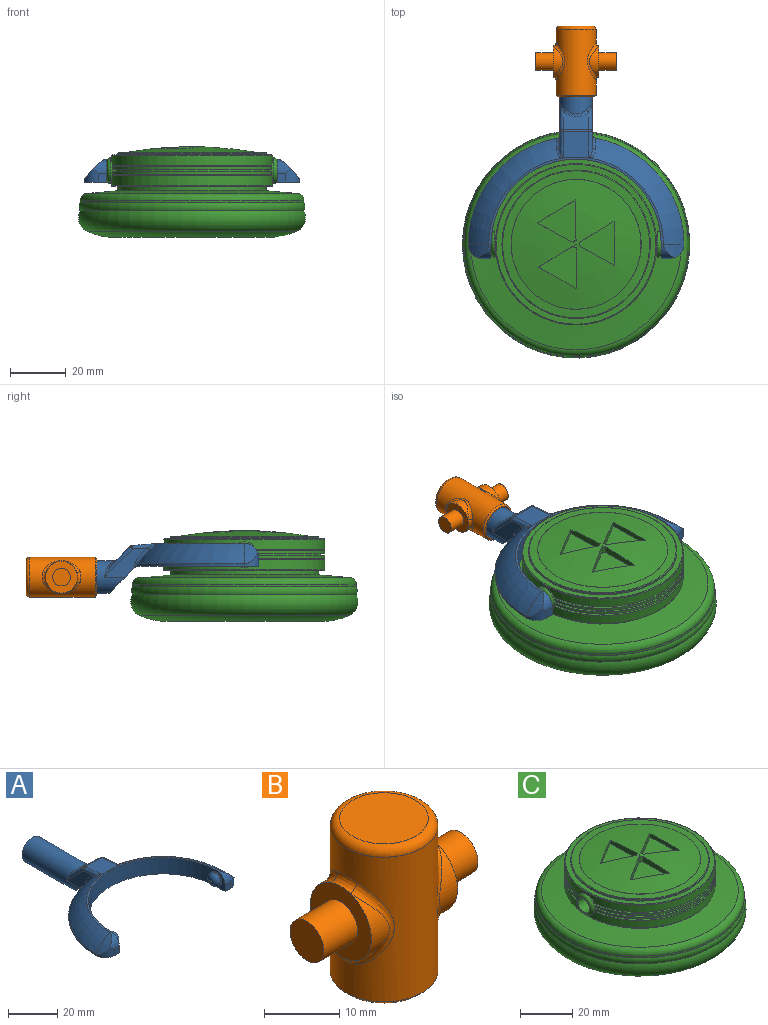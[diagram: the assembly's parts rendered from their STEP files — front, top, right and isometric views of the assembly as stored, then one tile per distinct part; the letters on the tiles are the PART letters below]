
ASSEMBLY  parts=3 mates=2
PART A: 48 faces, bbox 77.3x80.8x18.2 mm
  f0: plane 11.99x9.83mm, normal (0,-0.71,-0.71), area 141.5mm2, adj f1,f2,f9,f30,f43,f46
  f1: plane 15.39x10.49mm, normal (-1,0,0), area 63.5mm2, adj f0,f30,f32,f36,f46,f47
  f2: plane 15.39x10.49mm, normal (1,0,0), area 63.5mm2, adj f0,f30,f34,f39,f43,f44
  f3: plane 9.14x6.37mm, normal (0,0.71,0.71), area 67.6mm2, adj f35,f36,f39,f40
  f4: cylinder r=38.61mm len=37.99mm, axis (0,0,-1), area 42.6mm2, adj f6,f9,f17,f46,f47
  f5: torus R=19.3mm, axis (0,0,-1), area 507.8mm2, adj f10,f11,f12,f29,f42,f44
  f6: torus R=19.3mm, axis (0,0,-1), area 507.8mm2, adj f4,f11,f15,f28,f45,f47
  f7: cylinder r=30.48mm len=60.96mm, axis (0,0,-1), area 746.6mm2, adj f8,f9,f11,f14,f21,f24
  f8: plane 8.13x5.08mm, normal (-1,0,0), area 19.9mm2, adj f7,f9,f13,f19,f24
  f9: plane 77.22x43.73mm, normal (0,0,-1), area 956.2mm2, adj f0,f4,f7,f8,f10,f13,f14,f16
  f10: cylinder r=38.61mm len=37.99mm, axis (0,0,-1), area 42.6mm2, adj f5,f9,f20,f43,f44
  f11: plane 62.55x30.95mm, normal (0,0,1), area 75mm2, adj f5,f6,f7,f18,f19,f27
  f12: cylinder r=22.71mm len=7.33mm, axis (0,1,0), area 24.8mm2, adj f5,f19,f20
  f13: plane 3.05x3.05mm, normal (0,-1,0), area 9.3mm2, adj f8,f9,f19,f20
  f14: plane 8.13x5.08mm, normal (1,0,0), area 19.9mm2, adj f7,f9,f16,f18,f21
  f15: cylinder r=22.71mm len=7.33mm, axis (0,1,0), area 24.8mm2, adj f6,f17,f18
  f16: plane 3.05x3.05mm, normal (0,-1,0), area 9.3mm2, adj f9,f14,f17,f18
  f17: cylinder r=5.08mm len=5.08mm, axis (0,0,-1), area 21.9mm2, adj f4,f9,f15,f16,f18
  f18: cylinder r=5.08mm len=5.08mm, axis (-1,0,0), area 21.9mm2, adj f11,f14,f15,f16,f17
  f19: cylinder r=5.08mm len=5.08mm, axis (-1,0,0), area 21.9mm2, adj f8,f11,f12,f13,f20
  f20: cylinder r=5.08mm len=5.08mm, axis (0,0,-1), area 21.9mm2, adj f9,f10,f12,f13,f19
  f21: cylinder r=3.17mm len=6.35mm, axis (-1,0,0), area 12.7mm2, adj f7,f14,f23
  f22: plane 1.27x1.27mm, normal (1,0,0), area 1.3mm2, adj f23
  f23: torus R=0.64mm, axis (1,0,0), area 56.5mm2, adj f21,f22
  f24: cylinder r=3.17mm len=6.35mm, axis (1,0,0), area 12.7mm2, adj f7,f8,f26
  f25: plane 1.27x1.27mm, normal (-1,0,0), area 1.3mm2, adj f26
  f26: torus R=0.64mm, axis (-1,0,0), area 56.5mm2, adj f24,f25
  f27: plane 9.86x9.36mm, normal (0,0.09,1), area 85.6mm2, adj f11,f28,f29,f32,f34,f35,f42,f45
  f28: plane 1.04x0.17mm, normal (0,-1,0), area 0mm2, adj f6,f27,f45
  f29: plane 1.04x0.17mm, normal (0,-1,0), area 0mm2, adj f5,f27,f42
  f30: cylinder r=5.84mm len=33.01mm, axis (0,-1,0), area 1029.7mm2, adj f0,f1,f2,f31,f38,f40,f41
  f31: plane 11.68x11.68mm, normal (0,1,0), area 107.2mm2, adj f30
  f32: cylinder r=1.27mm len=9.13mm, axis (0,-1,0.09), area 14.4mm2, adj f1,f27,f33,f45
  f33: sphere r=1.27mm, area 1.5mm2, adj f32,f35,f36
  f34: cylinder r=1.27mm len=9.13mm, axis (0,1,-0.09), area 14.4mm2, adj f2,f27,f37,f42
  f35: cylinder r=1.27mm len=9.14mm, axis (-1,0,0), area 8.1mm2, adj f3,f27,f33,f37
  f36: cylinder r=1.27mm len=10.91mm, axis (0,-0.71,0.71), area 23.1mm2, adj f1,f3,f33,f38
  f37: sphere r=1.27mm, area 1.5mm2, adj f34,f35,f39
  f38: bspline ~4.55x2.75mm, area 2.3mm2, adj f30,f36,f40
  f39: cylinder r=1.27mm len=10.91mm, axis (0,0.71,-0.71), area 23.1mm2, adj f2,f3,f37,f41
  f40: bspline ~9.14x2.56mm, area 10.7mm2, adj f3,f30,f38,f41
  f41: bspline ~5.23x3.53mm, area 2.3mm2, adj f30,f39,f40
  f42: bspline ~4.62x3.14mm, area 5.2mm2, adj f5,f27,f29,f34,f44
  f43: cylinder r=1.27mm len=1.74mm, axis (0,0,-1), area 1.9mm2, adj f0,f2,f9,f10,f44
  f44: bspline ~8.6x7.86mm, area 11.9mm2, adj f2,f5,f10,f42,f43
  f45: bspline ~4.62x3.14mm, area 5.2mm2, adj f6,f27,f28,f32,f47
  f46: cylinder r=1.27mm len=1.74mm, axis (0,0,-1), area 1.9mm2, adj f0,f1,f4,f9,f47
  f47: bspline ~8.6x7.86mm, area 11.9mm2, adj f1,f4,f6,f45,f46
PART B: 25 faces, bbox 28.9x15.5x25.4 mm
  f0: cylinder r=5.71mm len=10.81mm, axis (-1,0,0), area 26.2mm2, adj f5,f15
  f1: cylinder r=5.71mm len=10.81mm, axis (-1,0,0), area 26.2mm2, adj f8,f11
  f2: cylinder r=7.14mm len=23.5mm, axis (0,0,-1), area 763.2mm2, adj f9,f10,f11,f12,f13,f14,f15,f16
  f3: plane 11.75x11.75mm, normal (0,0,1), area 108.4mm2, adj f17
  f4: plane 13.02x13.02mm, normal (0,0,-1), area 16.3mm2, adj f22,f24
  f5: plane 11.46x11.46mm, normal (1,0,0), area 70.9mm2, adj f0,f6,f13,f16,f18
  f6: cylinder r=5.71mm len=10.81mm, axis (-1,0,0), area 26.2mm2, adj f5,f14
  f7: cylinder r=5.71mm len=10.81mm, axis (-1,0,0), area 26.2mm2, adj f8,f10
  f8: plane 11.46x11.46mm, normal (-1,0,0), area 70.9mm2, adj f1,f7,f9,f12,f20
  f9: bspline ~4.64x1.73mm, area 6.5mm2, adj f2,f8,f10,f11
  f10: bspline ~13.62x4.91mm, area 20.7mm2, adj f2,f7,f9,f12
  f11: bspline ~13.6x4.87mm, area 20.7mm2, adj f1,f2,f9,f12
  f12: bspline ~4.64x1.73mm, area 6.5mm2, adj f2,f8,f10,f11
  f13: bspline ~4.64x1.73mm, area 6.5mm2, adj f2,f5,f14,f15
  f14: bspline ~13.62x4.91mm, area 20.7mm2, adj f2,f6,f13,f16
  f15: bspline ~13.6x4.87mm, area 20.7mm2, adj f0,f2,f13,f16
  f16: bspline ~4.64x1.73mm, area 6.5mm2, adj f2,f5,f14,f15
  f17: torus R=5.87mm, axis (0,0,1), area 83.8mm2, adj f2,f3
  f18: cylinder r=3.17mm len=6.35mm, axis (-1,0,0), area 126.7mm2, adj f5,f19
  f19: plane 6.35x6.35mm, normal (1,0,0), area 31.7mm2, adj f18
  f20: cylinder r=3.17mm len=6.35mm, axis (1,0,0), area 126.7mm2, adj f8,f21
  f21: plane 6.35x6.35mm, normal (-1,0,0), area 31.7mm2, adj f20
  f22: cylinder r=6.1mm len=22.86mm, axis (0,0,-1), area 875.6mm2, adj f4,f23
  f23: plane 12.19x12.19mm, normal (0,0,-1), area 116.7mm2, adj f22
  f24: cone r=7.14mm half-angle=45deg, axis (0,0,1), area 38.5mm2, adj f2,f4
PART C: 64 faces, bbox 96.2x96.2x32.5 mm
  f0: cylinder r=28.87mm len=57.73mm, axis (0,0,-1), area 603.9mm2, adj f1,f2,f54,f55,f60
  f1: plane 57.13x24.69mm, normal (0,0,1), area 102mm2, adj f0,f3,f54,f55
  f2: plane 57.13x24.69mm, normal (0,0,1), area 102mm2, adj f0,f4,f54,f55
  f3: cylinder r=27.6mm len=54.56mm, axis (0,0,1), area 49.6mm2, adj f1,f6,f54,f55
  f4: cylinder r=27.6mm len=54.56mm, axis (0,0,1), area 49.6mm2, adj f2,f5,f54,f55
  f5: plane 57.06x24.46mm, normal (0,0,-1), area 101.4mm2, adj f4,f7,f54,f55
  f6: plane 57.06x24.46mm, normal (0,0,-1), area 101.4mm2, adj f3,f8,f54,f55
  f7: cylinder r=28.87mm len=57.06mm, axis (0,0,-1), area 76.2mm2, adj f5,f10,f54,f55
  f8: cylinder r=28.87mm len=57.06mm, axis (0,0,-1), area 76.2mm2, adj f6,f9,f54,f55
  f9: plane 57.01x24.3mm, normal (0,0,1), area 101mm2, adj f8,f11,f54,f55
  f10: plane 57.01x24.3mm, normal (0,0,1), area 101mm2, adj f7,f12,f54,f55
  f11: cylinder r=27.6mm len=54.44mm, axis (0,0,1), area 49.2mm2, adj f9,f14,f54,f55
  f12: cylinder r=27.6mm len=54.44mm, axis (0,0,1), area 49.2mm2, adj f10,f13,f54,f55
  f13: plane 57.01x24.31mm, normal (0,0,-1), area 101mm2, adj f12,f15,f54,f55
  f14: plane 57.01x24.31mm, normal (0,0,-1), area 101mm2, adj f11,f16,f54,f55
  f15: cylinder r=28.87mm len=57.07mm, axis (0,0,-1), area 79.4mm2, adj f13,f18,f54,f55
  f16: cylinder r=28.87mm len=57.07mm, axis (0,0,-1), area 79.4mm2, adj f14,f17,f54,f55
  f17: plane 57.07x24.49mm, normal (0,0,1), area 101.5mm2, adj f16,f19,f54,f55
  f18: plane 57.07x24.49mm, normal (0,0,1), area 101.5mm2, adj f15,f20,f54,f55
  f19: cylinder r=27.6mm len=54.57mm, axis (0,0,1), area 49.6mm2, adj f17,f22,f54,f55
  f20: cylinder r=27.6mm len=54.57mm, axis (0,0,1), area 49.6mm2, adj f18,f21,f54,f55
  f21: plane 57.14x24.73mm, normal (0,0,-1), area 102.1mm2, adj f20,f23,f54,f55
  f22: plane 57.14x24.73mm, normal (0,0,-1), area 102.1mm2, adj f19,f23,f54,f55
  f23: cylinder r=28.87mm len=57.73mm, axis (0,0,-1), area 587.6mm2, adj f21,f22,f54,f55,f61
  f24: sphere r=135.39mm, area 1385.3mm2, adj f38,f39,f40,f41,f43,f44,f45,f46
  f25: plane 39.33x39.33mm, normal (0,0,-1), area 1214.6mm2, adj f26
  f26: torus R=20.12mm, axis (0,0,-1), area 1429.3mm2, adj f25,f27
  f27: torus R=27.74mm, axis (0,0,-1), area 3542.1mm2, adj f26,f28
  f28: torus R=35.36mm, axis (0,0,-1), area 2180.1mm2, adj f27,f29
  f29: torus R=37.35mm, axis (0,0,-1), area 734.6mm2, adj f28,f30
  f30: cylinder r=40.06mm len=80.11mm, axis (0,0,-1), area 213.3mm2, adj f29,f34
  f31: cone r=26.57mm half-angle=85deg, axis (0,0,-1), area 2265mm2, adj f32,f34
  f32: cylinder r=26.57mm len=53.14mm, axis (0,0,-1), area 265mm2, adj f31,f33
  f33: plane 57.23x57.23mm, normal (0,0,-1), area 354.5mm2, adj f32,f60
  f34: torus R=37.52mm, axis (0,0,1), area 928.6mm2, adj f30,f31
  f35: cone r=26.57mm half-angle=87deg, axis (0,0,-1), area 475.4mm2, adj f62,f63
  f36: cylinder r=26.57mm len=53.14mm, axis (0,0,-1), area 92.3mm2, adj f37,f62
  f37: plane 57.23x57.23mm, normal (0,0,1), area 354.5mm2, adj f36,f61
  f38: cylinder r=1.27mm len=2.53mm, axis (0,0,1), area 3.4mm2, adj f24,f39,f41,f42
  f39: plane 14.6x2.53mm, normal (-1,-0.02,0), area 32.2mm2, adj f24,f38,f40,f42
  f40: plane 13.58x8.22mm, normal (0.52,-0.86,0), area 28mm2, adj f24,f39,f41,f42
  f41: plane 12.8x7.04mm, normal (0.48,0.88,0), area 32.2mm2, adj f24,f38,f40,f42
  f42: plane 15.26x13.88mm, normal (0,0,1), area 108.3mm2, adj f38,f39,f40,f41
  f43: plane 14.6x2.53mm, normal (-1,-0.02,0), area 32.2mm2, adj f24,f44,f46,f47
  f44: cylinder r=1.27mm len=2.53mm, axis (0,0,1), area 3.4mm2, adj f24,f43,f45,f47
  f45: plane 12.5x7.56mm, normal (0.52,-0.86,0), area 32.2mm2, adj f24,f44,f46,f47
  f46: plane 13.91x7.65mm, normal (0.48,0.88,0), area 28mm2, adj f24,f43,f45,f47
  f47: plane 15.21x13.91mm, normal (0,0,1), area 108.3mm2, adj f43,f44,f45,f46
  f48: cylinder r=1.27mm len=2.53mm, axis (0,0,1), area 3.4mm2, adj f24,f49,f51,f52
  f49: plane 12.8x7.04mm, normal (0.48,0.88,0), area 32.2mm2, adj f24,f48,f50,f52
  f50: plane 15.87x1.84mm, normal (-1,-0.02,0), area 28mm2, adj f24,f49,f51,f52
  f51: plane 12.5x7.56mm, normal (0.52,-0.86,0), area 32.2mm2, adj f24,f48,f50,f52
  f52: plane 15.87x12.82mm, normal (0,0,1), area 108.3mm2, adj f48,f49,f50,f51
  f53: plane 6.6x6.6mm, normal (1,0,0), area 2.6mm2, adj f58,f59
  f54: cylinder r=4.57mm len=9.14mm, axis (-1,0,0), area 20.2mm2, adj f0,f1,f2,f3,f4,f5,f6,f7
  f55: cylinder r=4.57mm len=9.14mm, axis (-1,0,0), area 20.2mm2, adj f0,f1,f2,f3,f4,f5,f6,f7
  f56: plane 6.6x6.6mm, normal (-1,0,0), area 2.6mm2, adj f57,f59
  f57: torus R=3.3mm, axis (1,0,0), area 51.5mm2, adj f55,f56
  f58: torus R=3.3mm, axis (1,0,0), area 51.5mm2, adj f53,f54
  f59: cylinder r=3.17mm len=60.96mm, axis (1,0,0), area 1216.1mm2, adj f53,f56
  f60: torus R=28.61mm, axis (0,0,1), area 72.1mm2, adj f0,f33
  f61: torus R=28.61mm, axis (0,0,-1), area 72.1mm2, adj f23,f37
  f62: torus R=26.31mm, axis (0,0,1), area 64.2mm2, adj f35,f36
  f63: torus R=23.29mm, axis (0,0,1), area 4.5mm2, adj f24,f35
PLACE A t=(32.34,27.52,20.85)mm
PLACE B rot(axis=(-1,0,0),90deg) t=(32.34,80.3,16.88)mm
PLACE C t=(32.34,27.52,33.52)mm
MATE revolute A.f24 <-> C.f54  axis (-1,0,0) through (62.82,27.52,24.92)mm
MATE revolute B.f2 <-> A.f30  axis (0,-1,0) through (32.34,103.16,16.88)mm
